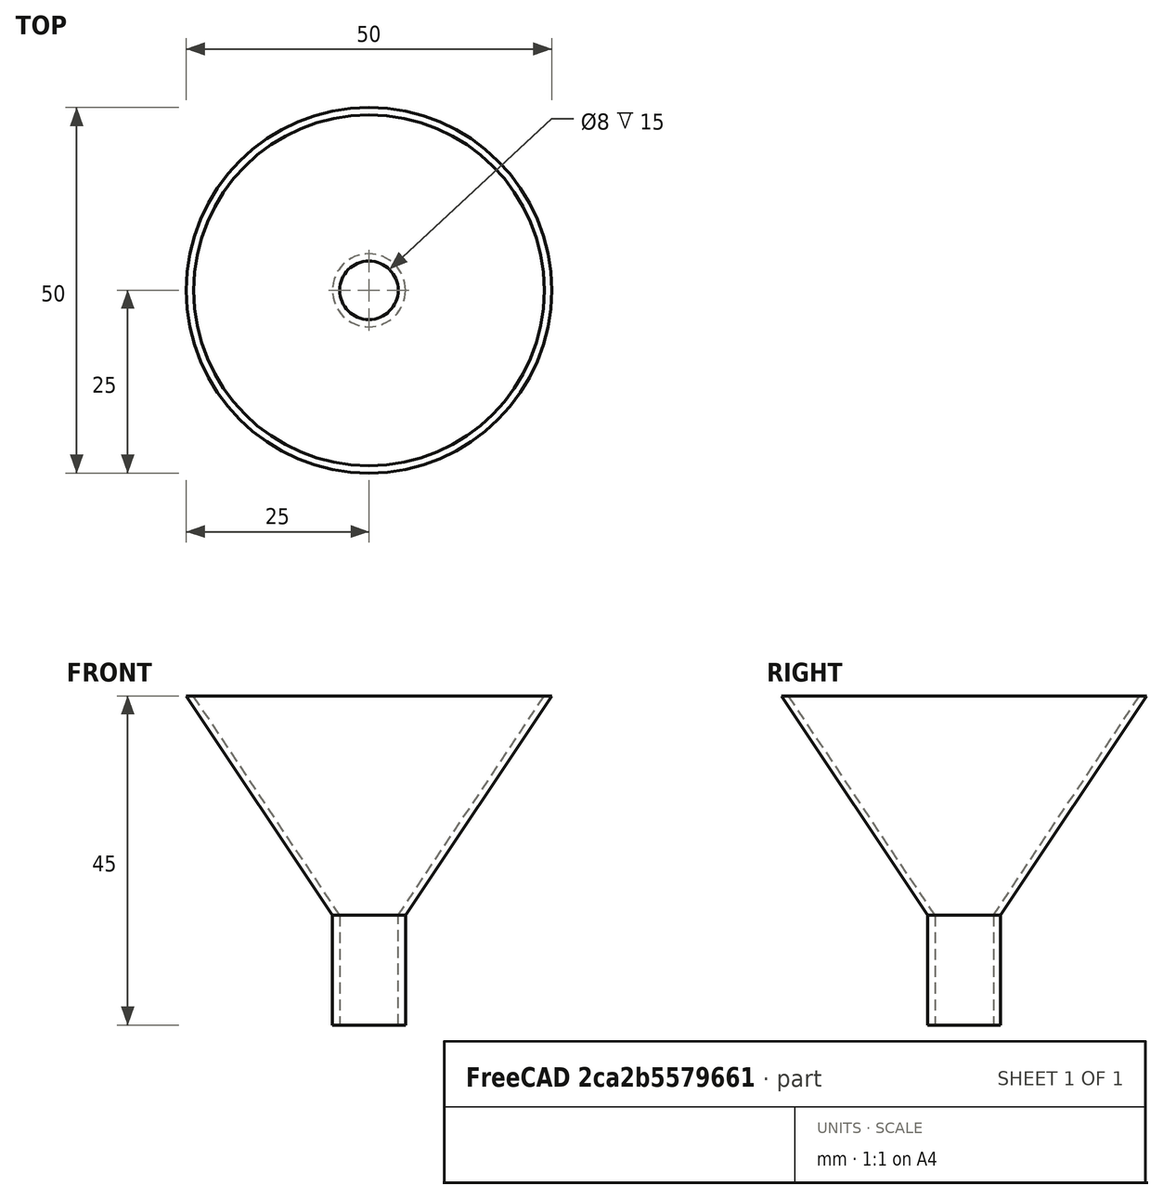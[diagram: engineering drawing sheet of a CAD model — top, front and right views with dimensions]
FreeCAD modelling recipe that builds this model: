
FCSTD DOCUMENT  (FreeCAD 0.21R33694 (Git))
Label: OJT1_T014_embudo
License: All rights reserved
LicenseURL: https://en.wikipedia.org/wiki/All_rights_reserved
objects: Part::Cone×2, Part::Cut×2, Part::Cylinder×2
note: 6 computed .brp shape members not serialized (recipe doc carries the construction recipe); baked Part::Feature solids carry a one-line shape summary decoded from their .brp

FEATURE [Part::Cone] Cone  label="Con"
  Angle = 360
  AttacherType = Attacher::AttachEngine3D
  Height = 30
  Radius1 = 5
  Radius2 = 25
FEATURE [Part::Cone] Cone001  label="Con001"
  Angle = 360
  AttacherType = Attacher::AttachEngine3D
  Height = 30
  Radius1 = 4
  Radius2 = 24
FEATURE [Part::Cut] Cut
  Base = -> Cone
  Tool = -> Cone001
FEATURE [Part::Cylinder] Cylinder  label="Cilindre"
  Angle = 360
  AttacherType = Attacher::AttachEngine3D
  FirstAngle = 0
  Height = 15
  Placement = pos=(0,0,-15) rot=(0,0,1;0rad)
  Radius = 5
  SecondAngle = 0
FEATURE [Part::Cylinder] Cylinder001  label="Cilindre001"
  Angle = 360
  AttacherType = Attacher::AttachEngine3D
  FirstAngle = 0
  Height = 15
  Placement = pos=(0,0,-15) rot=(0,0,1;0rad)
  Radius = 4
  SecondAngle = 0
  expr: .Placement.Base.y = 0
FEATURE [Part::Cut] Cut001
  Base = -> Cylinder
  Tool = -> Cylinder001
